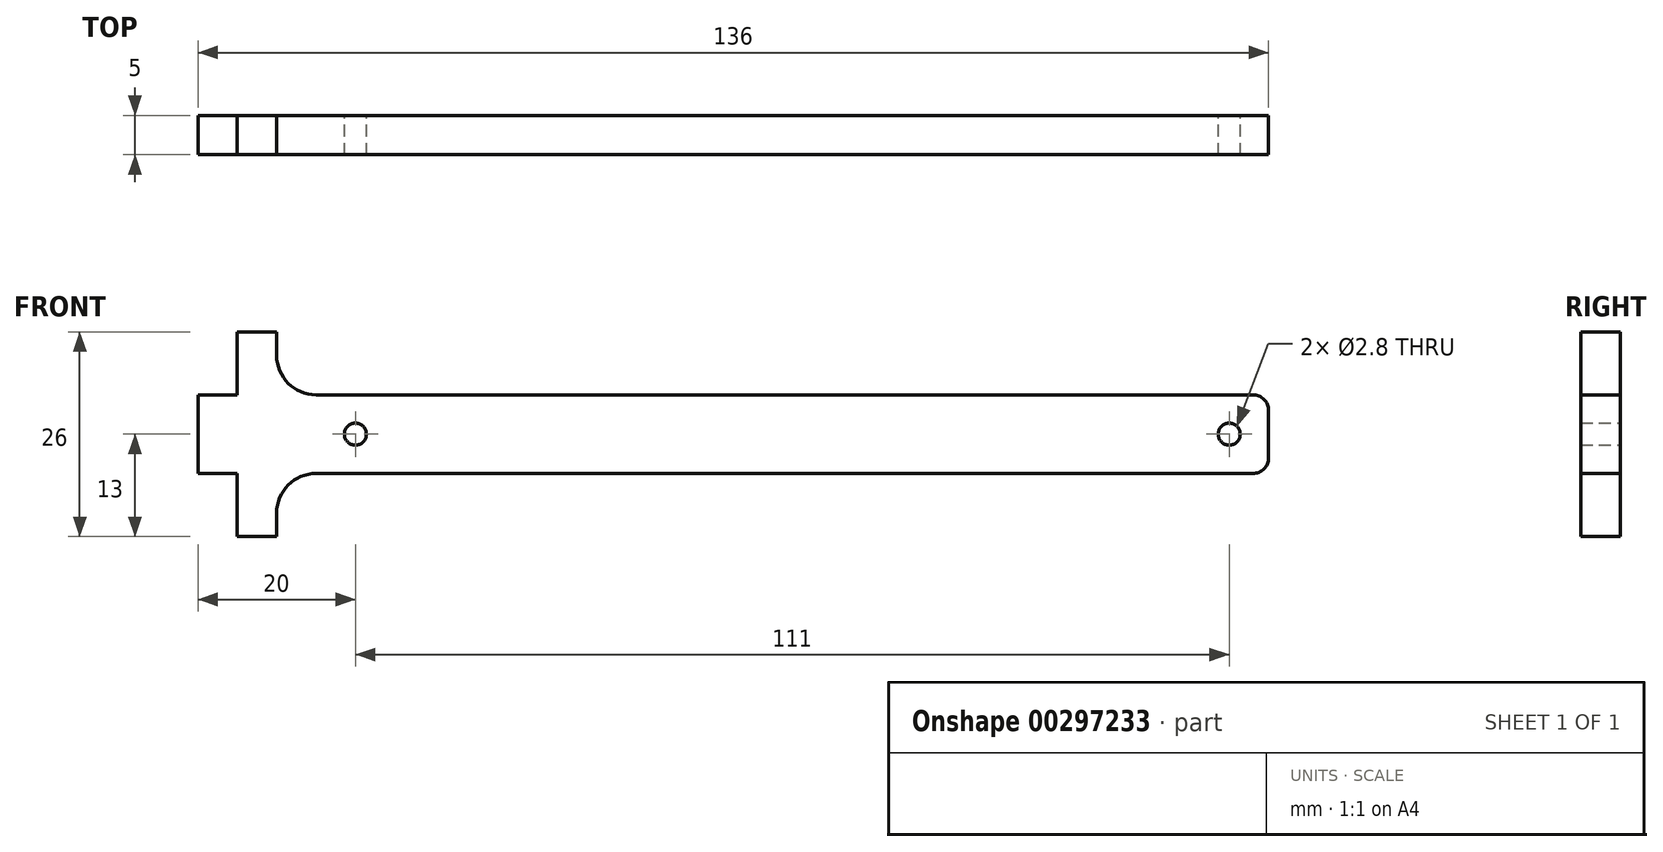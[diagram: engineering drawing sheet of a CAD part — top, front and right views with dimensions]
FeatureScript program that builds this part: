
annotation { "Feature Type Name" : "Feature", "Feature Type Description" : "" }
export const myFeature = defineFeature(function(context is Context, id is Id, definition is map)
    precondition{}
    {
        {
            var Q0;
            Q0=qCreatedBy(makeId("Front.planeOp"),FACE);
            var sketch = newSketch(context, id + "F0", { "sketchPlane" : qUnion([Q0])});
            skLineSegment(sketch, "E0.bottom", {"start": v(-5, -5) * mm, "end": v(114, -5) * mm});
            skLineSegment(sketch, "E0.top", {"start": v(-5, 5) * mm, "end": v(114, 5) * mm});
            skLineSegment(sketch, "E0.right", {"start": v(116, -3) * mm, "end": v(116, 3) * mm});
            skPoint(sketch, "E0.middle", {"position": v(50.5, 0) * mm});
            skCircle(sketch, "E1", {"center": v(0, 0) * mm, "radius": 1.4 * mm});
            skCircle(sketch, "E2", {"center": v(111, 0) * mm, "radius": 1.4 * mm});
            skPoint(sketch, "E3.visualSharp", {"position": v(116, 5) * mm});
            skArc(sketch, "E3.filletArc", {"start": v(116, 3) * mm, "mid": v(115.41, 4.41) * mm, "end": v(114, 5) * mm});
            skPoint(sketch, "E4.visualSharp", {"position": v(116, -5) * mm});
            skArc(sketch, "E4.filletArc", {"start": v(114, -5) * mm, "mid": v(115.41, -4.41) * mm, "end": v(116, -3) * mm});
            skLineSegment(sketch, "E5.bottom", {"start": v(-28.54, -25) * mm, "end": v(-33.54, -25) * mm});
            skLineSegment(sketch, "E5.top", {"start": v(-28.54, 25) * mm, "end": v(-33.54, 25) * mm});
            skLineSegment(sketch, "E5.left", {"start": v(-28.54, -25) * mm, "end": v(-28.54, 25) * mm});
            skLineSegment(sketch, "E5.right", {"start": v(-33.54, -25) * mm, "end": v(-33.54, 25) * mm});
            skPoint(sketch, "E5.middle", {"position": v(-31.04, 0) * mm});
            skLineSegment(sketch, "E6", {"start": v(-28.54, -25) * mm, "end": v(-23.54, -25) * mm});
            skLineSegment(sketch, "E7", {"start": v(-23.54, -25) * mm, "end": v(-23.54, 25) * mm});
            skLineSegment(sketch, "E8", {"start": v(-23.54, 25) * mm, "end": v(-28.54, 25) * mm});
            skLineSegment(sketch, "E9.bottom", {"start": v(-20, 5) * mm, "end": v(-15, 5) * mm});
            skLineSegment(sketch, "E9.top", {"start": v(-20, -5) * mm, "end": v(-15, -5) * mm});
            skLineSegment(sketch, "E9.left", {"start": v(-20, 5) * mm, "end": v(-20, -5) * mm});
            skPoint(sketch, "E9.middle", {"position": v(-17.5, 0) * mm});
            skPoint(sketch, "E9.middle.positionSnap0", {"position": v(-23.54, 0) * mm});
            skPoint(sketch, "E9.centerSnap0", {"position": v(-23.54, 0) * mm});
            skLineSegment(sketch, "E10.bottom", {"start": v(-10, -13) * mm, "end": v(-15, -13) * mm});
            skLineSegment(sketch, "E10.top", {"start": v(-10, 13) * mm, "end": v(-15, 13) * mm});
            skLineSegment(sketch, "E10.left", {"start": v(-10, 10) * mm, "end": v(-10, 13) * mm});
            skLineSegment(sketch, "E10.right", {"start": v(-15, -13) * mm, "end": v(-15, -5) * mm});
            skArc(sketch, "E11.filletArc", {"start": v(-10, 10) * mm, "mid": v(-8.54, 6.46) * mm, "end": v(-5, 5) * mm});
            skLineSegment(sketch, "E12", {"start": v(-10, -13) * mm, "end": v(-10, -10) * mm});
            skArc(sketch, "E13.filletArc", {"start": v(-5, -5) * mm, "mid": v(-8.54, -6.46) * mm, "end": v(-10, -10) * mm});
            skLineSegment(sketch, "E14.trimOffspring", {"start": v(-15, 5) * mm, "end": v(-15, 13) * mm});
            skSolve(sketch);
        }
        {
            var Q0;
            Q0=makeQuery(id+"F0.imprint","IMPRINT",FACE,{"disambiguationData":[TD([[makeQuery(id+"F0.imprint","IMPRINT",EDGE,{"derivedFrom":sQuery(id+"F0.wireOp",EDGE,"E0.bottom")}),1.0]])]});
            extrude(context, id + "F1", {"entities" : qUnion([Q0]), "depth" : 5 * mm});
        }
    });
